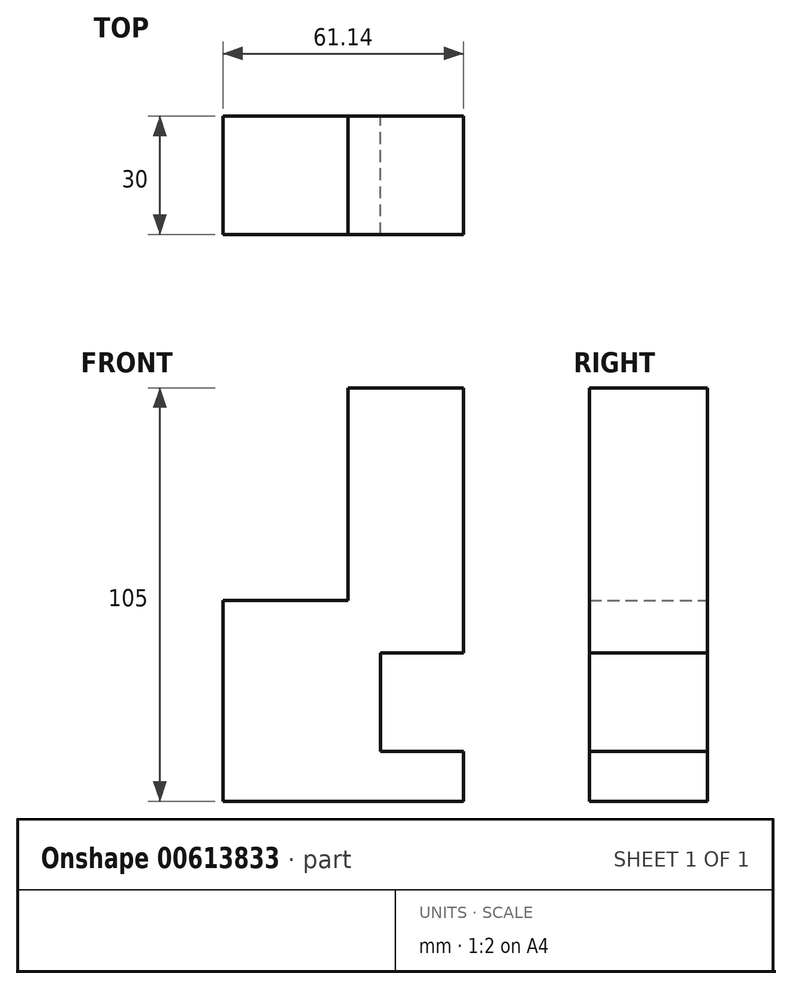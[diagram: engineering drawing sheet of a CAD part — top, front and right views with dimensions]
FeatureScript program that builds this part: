
annotation { "Feature Type Name" : "Feature", "Feature Type Description" : "" }
export const myFeature = defineFeature(function(context is Context, id is Id, definition is map)
    precondition{}
    {
        {
            var Q0;
            Q0=qCreatedBy(makeId("Front.planeOp"),FACE);
            var sketch = newSketch(context, id + "F0", { "sketchPlane" : qUnion([Q0])});
            skLineSegment(sketch, "E0.bottom", {"start": v(-8.26, 54) * mm, "end": v(21.14, 54) * mm});
            skLineSegment(sketch, "E0.top", {"start": v(-8.26, -51) * mm, "end": v(21.14, -51) * mm});
            skLineSegment(sketch, "E0.left", {"start": v(-8.26, 54) * mm, "end": v(-8.26, 0) * mm});
            skLineSegment(sketch, "E0.right", {"start": v(21.14, 54) * mm, "end": v(21.14, -13.38) * mm});
            skLineSegment(sketch, "E1.bottom", {"start": v(-8.26, 0) * mm, "end": v(-40, 0) * mm});
            skLineSegment(sketch, "E1.top", {"start": v(-8.26, -51) * mm, "end": v(-40, -51) * mm});
            skLineSegment(sketch, "E1.right", {"start": v(-40, 0) * mm, "end": v(-40, -51) * mm});
            skLineSegment(sketch, "E2.bottom", {"start": v(21.14, -13.38) * mm, "end": v(0, -13.38) * mm});
            skLineSegment(sketch, "E2.top", {"start": v(21.14, -38.38) * mm, "end": v(0, -38.38) * mm});
            skLineSegment(sketch, "E2.right", {"start": v(0, -13.38) * mm, "end": v(0, -38.38) * mm});
            skLineSegment(sketch, "E3.trimOffspring", {"start": v(21.14, -38.38) * mm, "end": v(21.14, -51) * mm});
            skSolve(sketch);
        }
        {
            var Q0;
            Q0 = qSketchRegion(id + "F0", true);
            extrude(context, id + "F1", {"entities" : qUnion([Q0]), "depth" : 30 * mm, "offsetDistance" : 25 * mm});
        }
    });
